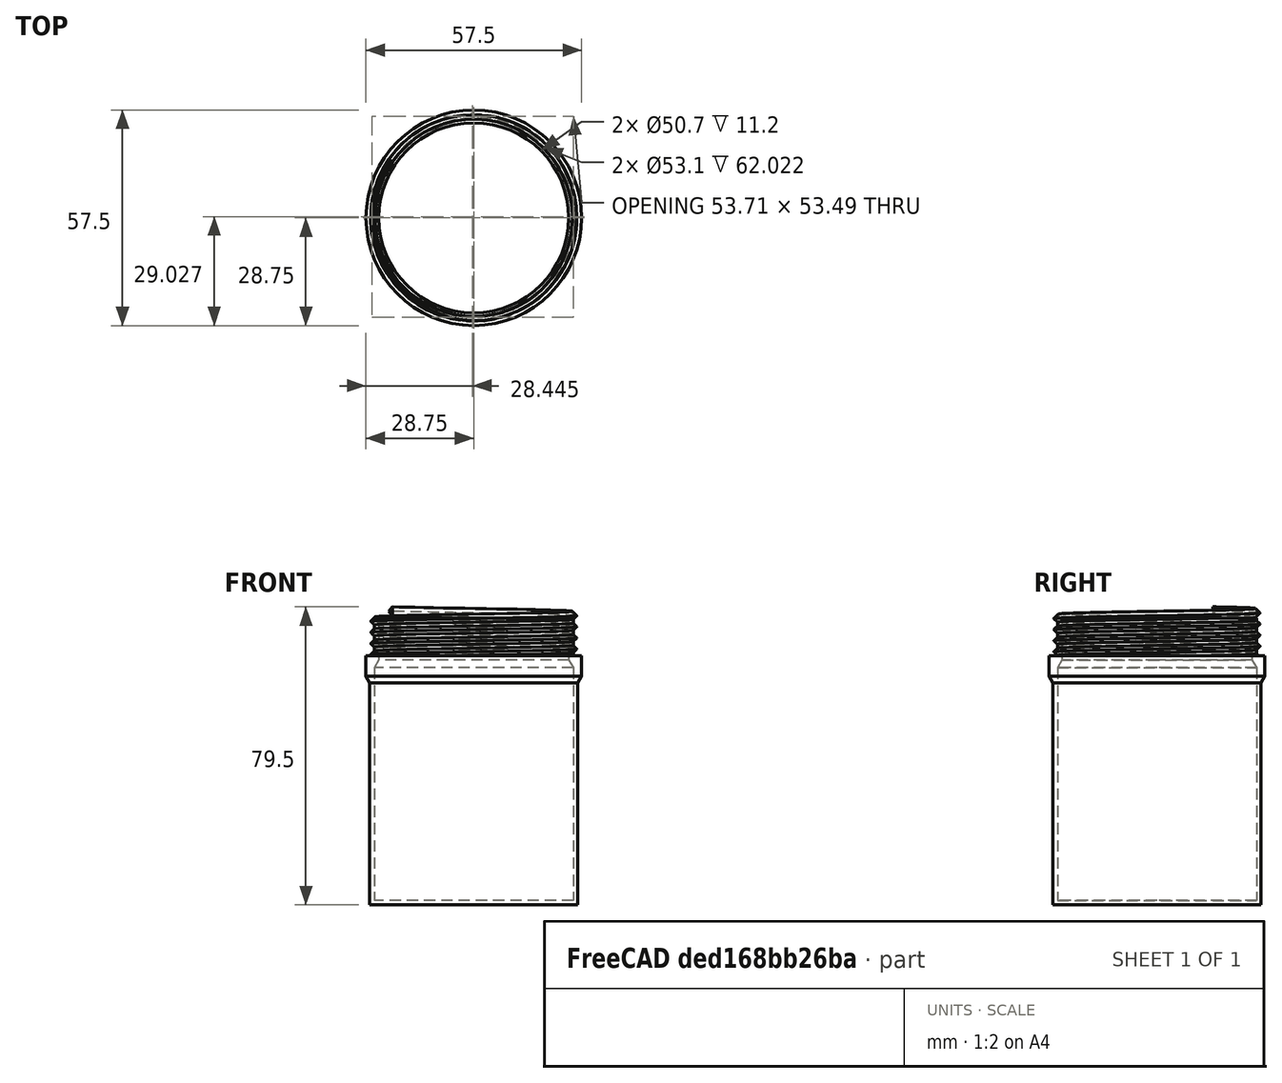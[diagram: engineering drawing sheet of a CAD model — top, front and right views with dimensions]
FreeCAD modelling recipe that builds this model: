
FCSTD DOCUMENT  (FreeCAD 0.21R33694 (Git))
Label: gewuerzdose_fuchs
License: All rights reserved
LicenseURL: http://en.wikipedia.org/wiki/All_rights_reserved
objects: Sketcher::SketchObject×5, PartDesign::Revolution×3, PartDesign::Body×3, Part::FeaturePython×3, PartDesign::Fillet×2, Mesh::Feature×2, PartDesign::AdditiveHelix×1, PartDesign::Plane×1, App::DocumentObjectGroup×1, PartDesign::FeatureBase×1, Spreadsheet::Sheet×1, PartDesign::SubtractiveHelix×1
note: 27 computed .brp shape members not serialized (recipe doc carries the construction recipe); baked Part::Feature solids carry a one-line shape summary decoded from their .brp

FEATURE [Sketcher::SketchObject] Sketch
  FullyConstrained = true
  MapMode = 5
  Placement = pos=(0,0,0) rot=(1,0,0;1.5708rad)
  Support = -> [XZ_Plane]
  expr: Constraints[23] = <<dimensions>>.case_diameter / 2
  expr: Constraints[24] = <<dimensions>>.case_thickness
  expr: Constraints[25] = <<dimensions>>.case_thickness
  expr: Constraints[26] = <<dimensions>>.case_thickness
  expr: Constraints[27] = <<dimensions>>.case_height
  expr: Constraints[28] = <<dimensions>>.cap_height
  expr: Constraints[29] = 180 - <<dimensions>>.angle
  expr: Constraints[30] = 180 - <<dimensions>>.angle
  expr: Constraints[31] = <<dimensions>>.case_caplip
  expr: Constraints[33] = <<dimensions>>.case_overhang
  expr: Constraints[34] = <<dimensions>>.case_thickness
  sketch-geometry (12):
    g0: LineSegment StartX=0 StartY=0 StartZ=0 EndX=27.75 EndY=0 EndZ=0
    g1: LineSegment StartX=27.75 StartY=0 StartZ=0 EndX=27.75 EndY=59.2679 EndZ=0
    g2: LineSegment StartX=27.75 StartY=59.2679 StartZ=0 EndX=28.75 EndY=61 EndZ=0
    g3: LineSegment StartX=28.75 StartY=61 StartZ=0 EndX=28.75 EndY=66.5 EndZ=0
    g4: LineSegment StartX=28.75 StartY=66.5 StartZ=0 EndX=26.55 EndY=66.5 EndZ=0
    g5: LineSegment StartX=26.55 StartY=66.5 StartZ=0 EndX=26.55 EndY=76.5 EndZ=0
    g6: LineSegment StartX=26.55 StartY=76.5 StartZ=0 EndX=25.35 EndY=76.5 EndZ=0
    g7: LineSegment StartX=25.35 StartY=76.5 StartZ=0 EndX=25.35 EndY=65.3 EndZ=0
    g8: LineSegment StartX=25.35 StartY=65.3 StartZ=0 EndX=26.55 EndY=63.2215 EndZ=0
    g9: LineSegment StartX=26.55 StartY=63.2215 StartZ=0 EndX=26.55 EndY=1.2 EndZ=0
    g10: LineSegment StartX=26.55 StartY=1.2 StartZ=0 EndX=0 EndY=1.2 EndZ=0
    g11: LineSegment StartX=0 StartY=1.2 StartZ=0 EndX=0 EndY=0 EndZ=0
  constraints (35):
    c: Coincident(g-1,g0)
    c: Horizontal(g0)
    c: Coincident(g0,g1)
    c: Vertical(g1)
    c: Coincident(g1,g2)
    c: Coincident(g2,g3)
    c: Vertical(g3)
    c: Coincident(g3,g4)
    c: Horizontal(g4)
    c: Coincident(g4,g5)
    c: Vertical(g5)
    c: Coincident(g5,g6)
    c: Horizontal(g6)
    c: Coincident(g6,g7)
    c: Vertical(g7)
    c: Coincident(g7,g8)
    c: Coincident(g8,g9)
    c: Vertical(g9)
    c: Coincident(g9,g10)
    c: PointOnObject(g10,g-2)
    c: Horizontal(g10)
    c: Coincident(g10,g11)
    c: Coincident(g11,g0)
    c: DistanceX(g0,g0) = 27.75
    c: DistanceY(g11,g11) = 1.2
    c: Distance(g9,g1) = 1.2
    c: DistanceX(g6,g6) = 1.2
    c: DistanceY(g0,g5) = 76.5
    c: DistanceY(g5,g5) = 10
    c: Angle(g1,g2) = 2.61799
    c: Angle(g8,g9) = 2.61799
    c: DistanceY(g3,g3) = 5.5
    c: Vertical(g8,g4)
    c: DistanceX(g1,g2) = 1
    c: DistanceY(g7,g4) = 1.2
FEATURE [PartDesign::Revolution] Revolution
  Angle = 360
  Axis = (0,-2e-16,1)
  Base = (0,0,0)
  Placement = pos=(0,0,0) rot=(1,0,0;1.5708rad)
  Profile = -> Sketch
  ReferenceAxis = -> Sketch [V_Axis]
  Reversed = true
FEATURE [Sketcher::SketchObject] Sketch001
  FullyConstrained = true
  MapMode = 5
  Placement = pos=(0,0,0) rot=(1,0,0;1.5708rad)
  Support = -> [XZ_Plane]
  expr: Constraints[4] = <<dimensions>>.thread_angle
  expr: Constraints[5] = <<dimensions>>.thread_height
  expr: Constraints[7] = <<dimensions>>.case_height - <<dimensions>>.cap_height - <<dimensions>>.thread_height
  expr: Constraints[8] = <<dimensions>>.case_diameter / 2 - <<dimensions>>.case_thickness - <<dimensions>>.tolerance / 2
  sketch-geometry (3):
    g0: LineSegment StartX=26.3 StartY=66.5 StartZ=0 EndX=26.3 EndY=64.1 EndZ=0
    g1: LineSegment StartX=26.3 StartY=64.1 StartZ=0 EndX=27.5 EndY=65.3 EndZ=0
    g2: LineSegment StartX=27.5 StartY=65.3 StartZ=0 EndX=26.3 EndY=66.5 EndZ=0
  constraints (9):
    c: Vertical(g0)
    c: Coincident(g0,g1)
    c: Coincident(g1,g2)
    c: Coincident(g2,g0)
    c: Angle(g1,g0) = 0.785398
    c: DistanceY(g0,g0) = 2.4
    c: Equal(g1,g2)
    c: DistanceY(g-1,g0) = 64.1
    c: DistanceX(g-1,g0) = 26.3
FEATURE [PartDesign::AdditiveHelix] AdditiveHelix
  Angle = 0
  Axis = (0,-2e-16,1)
  Base = (0,0,0)
  BaseFeature = -> Revolution
  Growth = 0
  HasBeenEdited = true
  Height = 13
  LeftHanded = false
  Mode = 0
  Outside = false
  Pitch = 2.95161
  Placement = pos=(0,0,0) rot=(1,0,0;1.5708rad)
  Profile = -> Sketch001
  ReferenceAxis = -> Sketch001 [V_Axis]
  Turns = 4.40438
FEATURE [PartDesign::Plane] DatumPlane
  Length = 64.1182
  MapMode = 2
  Placement = pos=(0,0,76.5) rot=(0,0,1;0rad)
  ResizeMode = 0
  Width = 60.3682
  expr: .Placement.Base.z = <<dimensions>>.case_height
FEATURE [PartDesign::Body] Body  label="case_all"
  Group = -> [Sketch,Revolution,Sketch001,AdditiveHelix,DatumPlane]
  Origin = -> Origin
  Tip = -> AdditiveHelix
FEATURE [Part::FeaturePython] Slice  # WARN: FeaturePython — macro-defined, semantics opaque (R4)
  Base = -> AdditiveHelix
  Mode = 1
  Tolerance = 0
  Tools = -> [DatumPlane]
FEATURE [Part::FeaturePython] Slice_child0  label="Slice.0"  # WARN: FeaturePython — macro-defined, semantics opaque (R4)
  Base = -> Slice
  FilterType = 1
  Invert = false
  OverrideMaxVal = 0
  WindowFrom = 80
  WindowTo = 100
  items = 0
FEATURE [Part::FeaturePython] Slice_child1  label="Slice.1"  # WARN: FeaturePython — macro-defined, semantics opaque (R4)
  Base = -> Slice
  FilterType = 1
  Invert = false
  OverrideMaxVal = 0
  WindowFrom = 80
  WindowTo = 100
  items = 1
FEATURE [App::DocumentObjectGroup] GrExplode_Slice  label="case_split"
  Group = -> [Slice_child0,Slice_child1]
FEATURE [PartDesign::FeatureBase] BaseFeature
  BaseFeature = -> Slice_child0
FEATURE [PartDesign::Fillet] Fillet
  Base = -> BaseFeature [Edge1]
  BaseFeature = -> BaseFeature
  Radius = 1
  SupportTransform = false
  UseAllEdges = false
FEATURE [PartDesign::Body] Body001  label="case"
  BaseFeature = -> Slice_child0
  Group = -> [BaseFeature,Fillet]
  Origin = -> Origin001
  Tip = -> Fillet
FEATURE [Sketcher::SketchObject] Sketch002
  FullyConstrained = true
  MapMode = 5
  Placement = pos=(0,0,0) rot=(1,0,0;1.5708rad)
  Support = -> [XZ_Plane002]
  expr: Constraints[10] = <<dimensions>>.case_height + <<dimensions>>.tolerance / 2
  expr: Constraints[11] = <<dimensions>>.case_diameter / 2 + <<dimensions>>.case_overhang
  expr: Constraints[8] = <<dimensions>>.case_thickness + <<dimensions>>.case_overhang - <<dimensions>>.tolerance / 2
  expr: Constraints[9] = <<dimensions>>.cap_height + <<dimensions>>.tolerance / 2
  sketch-geometry (4):
    g0: LineSegment StartX=26.8 StartY=76.75 StartZ=0 EndX=28.75 EndY=76.75 EndZ=0
    g1: LineSegment StartX=28.75 StartY=76.75 StartZ=0 EndX=28.75 EndY=66.5 EndZ=0
    g2: LineSegment StartX=28.75 StartY=66.5 StartZ=0 EndX=26.8 EndY=66.5 EndZ=0
    g3: LineSegment StartX=26.8 StartY=66.5 StartZ=0 EndX=26.8 EndY=76.75 EndZ=0
  constraints (12):
    c: Coincident(g0,g1)
    c: Coincident(g1,g2)
    c: Coincident(g2,g3)
    c: Coincident(g3,g0)
    c: Horizontal(g0)
    c: Horizontal(g2)
    c: Vertical(g1)
    c: Vertical(g3)
    c: DistanceX(g2,g2) = 1.95
    c: DistanceY(g1,g1) = 10.25
    c: DistanceY(g-1,g0) = 76.75
    c: DistanceX(g-1,g0) = 28.75
FEATURE [Sketcher::SketchObject] Sketch003
  FullyConstrained = true
  MapMode = 5
  Placement = pos=(0,0,0) rot=(1,0,0;1.5708rad)
  Support = -> [XZ_Plane002]
  expr: Constraints[5] = <<dimensions>>.thread_angle
  expr: Constraints[6] = <<dimensions>>.thread_height
  expr: Constraints[7] = <<dimensions>>.case_diameter / 2 - <<dimensions>>.case_thickness + <<dimensions>>.tolerance / 2
  expr: Constraints[8] = <<dimensions>>.case_height - <<dimensions>>.cap_height - <<dimensions>>.thread_height
  sketch-geometry (3):
    g0: LineSegment StartX=26.8 StartY=66.5 StartZ=0 EndX=26.8 EndY=64.1 EndZ=0
    g1: LineSegment StartX=26.8 StartY=64.1 StartZ=0 EndX=28 EndY=65.3 EndZ=0
    g2: LineSegment StartX=28 StartY=65.3 StartZ=0 EndX=26.8 EndY=66.5 EndZ=0
  constraints (9):
    c: Vertical(g0)
    c: Coincident(g0,g1)
    c: Coincident(g1,g2)
    c: Coincident(g2,g0)
    c: Equal(g1,g2)
    c: Angle(g1,g0) = 0.785398
    c: DistanceY(g0,g0) = 2.4
    c: DistanceX(g-1,g0) = 26.8
    c: DistanceY(g-1,g0) = 64.1
FEATURE [Spreadsheet::Sheet] Spreadsheet  label="dimensions"
  cells = A1='case_diameter; B1(case_diameter)==55.5 mm; A2='case_thickness; B2(case_thickness)==1.2 mm; A3='case_height; B3(case_height)==76.5 mm; A4='case_overhang; B4(case_overhang)==1 mm; A5='case_caplip; B5(case_caplip)==5.5 mm; A6='cap_height; B6(cap_height)==10 mm; A7='cap_thickness; B7(cap_thickness)==1.2 mm; A8='thread_height; B8(thread_height)==2.4 mm; A9='thread_angle; B9(thread_angle)=45; A10='tolerance; B10(tolerance)==0.5 mm; A11='angle; B11(angle)=30
FEATURE [PartDesign::Revolution] Revolution001
  Angle = 360
  Axis = (0,-2e-16,1)
  Base = (0,0,0)
  Placement = pos=(0,0,0) rot=(1,0,0;1.5708rad)
  Profile = -> Sketch002
  ReferenceAxis = -> Sketch002 [V_Axis]
  Reversed = true
FEATURE [PartDesign::SubtractiveHelix] SubtractiveHelix
  Angle = 0
  Axis = (0,-2e-16,1)
  Base = (0,0,0)
  BaseFeature = -> Revolution001
  Growth = 0
  HasBeenEdited = true
  Height = 13
  LeftHanded = false
  Mode = 0
  Outside = false
  Pitch = 2.95161
  Placement = pos=(0,0,0) rot=(1,0,0;1.5708rad)
  Profile = -> Sketch003
  ReferenceAxis = -> Sketch003 [V_Axis]
  Turns = 4.40438
FEATURE [Sketcher::SketchObject] Sketch004
  FullyConstrained = true
  MapMode = 5
  Placement = pos=(0,0,0) rot=(1,0,0;1.5708rad)
  Support = -> [XZ_Plane002]
  expr: Constraints[10] = <<dimensions>>.case_diameter / 2 + <<dimensions>>.case_overhang
  expr: Constraints[11] = <<dimensions>>.case_height + <<dimensions>>.tolerance / 2
  expr: Constraints[9] = <<dimensions>>.cap_thickness
  sketch-geometry (4):
    g0: LineSegment StartX=0 StartY=77.95 StartZ=0 EndX=28.75 EndY=77.95 EndZ=0
    g1: LineSegment StartX=28.75 StartY=77.95 StartZ=0 EndX=28.75 EndY=76.75 EndZ=0
    g2: LineSegment StartX=28.75 StartY=76.75 StartZ=0 EndX=0 EndY=76.75 EndZ=0
    g3: LineSegment StartX=0 StartY=76.75 StartZ=0 EndX=0 EndY=77.95 EndZ=0
  constraints (12):
    c: Coincident(g0,g1)
    c: Coincident(g1,g2)
    c: Coincident(g2,g3)
    c: Coincident(g3,g0)
    c: Horizontal(g0)
    c: Horizontal(g2)
    c: Vertical(g1)
    c: Vertical(g3)
    c: PointOnObject(g0,g-2)
    c: DistanceY(g1,g1) = 1.2
    c: DistanceX(g0,g0) = 28.75
    c: DistanceY(g-1,g2) = 76.75
FEATURE [PartDesign::Revolution] Revolution002
  Angle = 360
  Axis = (0,-2e-16,1)
  Base = (0,0,0)
  BaseFeature = -> SubtractiveHelix
  Placement = pos=(0,0,0) rot=(1,0,0;1.5708rad)
  Profile = -> Sketch004
  ReferenceAxis = -> Sketch004 [V_Axis]
  Reversed = true
FEATURE [PartDesign::Fillet] Fillet001
  Base = -> Revolution002 [Edge8]
  BaseFeature = -> Revolution002
  Placement = pos=(0,0,0) rot=(1,0,0;1.5708rad)
  Radius = 1
  SupportTransform = false
  UseAllEdges = false
FEATURE [PartDesign::Body] Body002  label="cap"
  Group = -> [Sketch002,Revolution001,Sketch003,SubtractiveHelix,Sketch004,Revolution002,Fillet001]
  Origin = -> Origin002
  Tip = -> Fillet001
FEATURE [Mesh::Feature] Mesh  label="case (Meshed)"
FEATURE [Mesh::Feature] Mesh001  label="cap (Meshed)"
